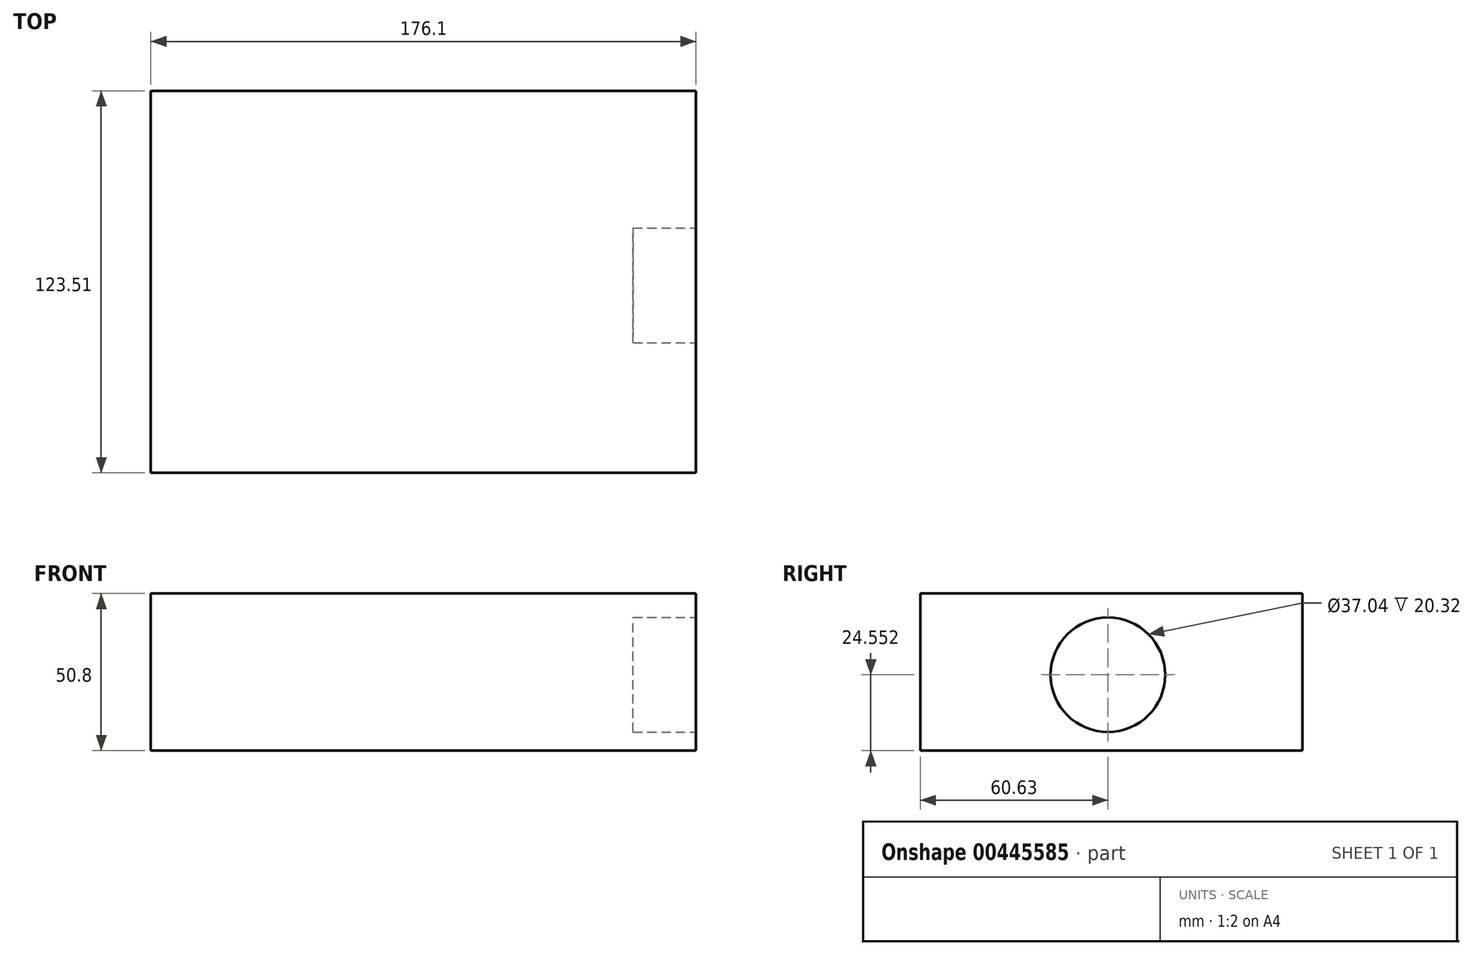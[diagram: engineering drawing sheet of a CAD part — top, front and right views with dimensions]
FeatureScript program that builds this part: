
annotation { "Feature Type Name" : "Feature", "Feature Type Description" : "" }
export const myFeature = defineFeature(function(context is Context, id is Id, definition is map)
    precondition{}
    {
        {
            var Q0;
            Q0=qCreatedBy(makeId("Top.planeOp"),FACE);
            var sketch = newSketch(context, id + "F0", { "sketchPlane" : qUnion([Q0])});
            skLineSegment(sketch, "E0.bottom", {"start": v(-114.3, 62.88) * mm, "end": v(61.8, 62.88) * mm});
            skLineSegment(sketch, "E0.top", {"start": v(-114.3, -60.63) * mm, "end": v(61.8, -60.63) * mm});
            skLineSegment(sketch, "E0.left", {"start": v(-114.3, 62.88) * mm, "end": v(-114.3, -60.63) * mm});
            skLineSegment(sketch, "E0.right", {"start": v(61.8, 62.88) * mm, "end": v(61.8, -60.63) * mm});
            skSolve(sketch);
        }
        {
            var Q0;
            Q0 = qSketchRegion(id + "F0", true);
            extrude(context, id + "F1", {"entities" : qUnion([Q0]), "depth" : 50.8 * mm});
        }
        {
            var Q0;
            Q0=makeQuery(id+"F1.opExtrude","SWEPT_FACE",FACE,{"disambiguationData":[OSD([sQuery(id+"F0.wireOp",EDGE,"E0.right")])]});
            var sketch = newSketch(context, id + "F2", { "sketchPlane" : qUnion([Q0])});
            skCircle(sketch, "E1", {"center": v(0, 24.55) * mm, "radius": 18.52 * mm});
            skSolve(sketch);
        }
        {
            var Q0;
            Q0 = qSketchRegion(id + "F2", true);
            extrude(context, id + "F3", {"entities" : qUnion([Q0]), "operationType" : NewBodyOperationType.REMOVE, "oppositeDirection" : true, "depth" : 20.32 * mm});
        }
    });
